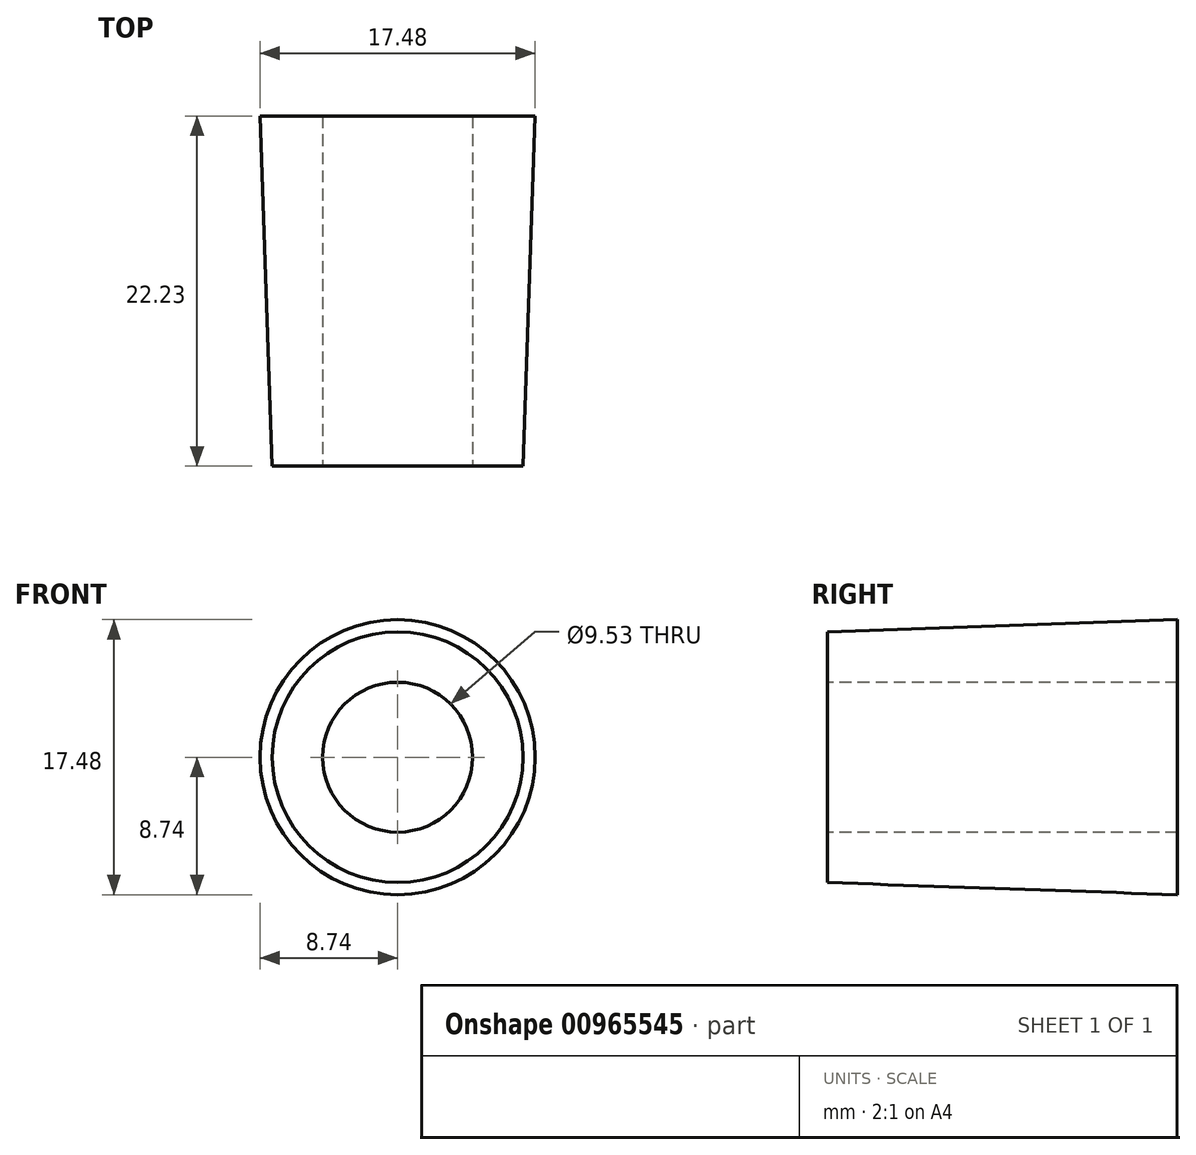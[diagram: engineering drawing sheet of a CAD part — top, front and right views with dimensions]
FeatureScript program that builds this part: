
annotation { "Feature Type Name" : "Feature", "Feature Type Description" : "" }
export const myFeature = defineFeature(function(context is Context, id is Id, definition is map)
    precondition{}
    {
        {
            var Q0;
            Q0=qCreatedBy(makeId("Right.planeOp"),FACE);
            var sketch = newSketch(context, id + "F0", { "sketchPlane" : qUnion([Q0])});
            skLineSegment(sketch, "E0", {"start": v(5.87, 0) * mm, "end": v(165.81, 0) * mm, "construction": true});
            skLineSegment(sketch, "E1", {"start": v(0, 4.76) * mm, "end": v(0, 7.96) * mm});
            skLineSegment(sketch, "E2", {"start": v(0, 7.96) * mm, "end": v(22.22, 8.74) * mm});
            skLineSegment(sketch, "E3", {"start": v(22.23, 8.74) * mm, "end": v(22.23, 4.76) * mm});
            skLineSegment(sketch, "E4", {"start": v(22.23, 4.76) * mm, "end": v(0, 4.76) * mm});
            skSolve(sketch);
        }
        {
            var Q0;
            Q0 = qSketchRegion(id + "F0", true);
            var Q1;
            Q1=sQuery(id+"F0.wireOp",EDGE,"E0");
            revolve(context, id + "F1", {"surfaceOperationType" : NewSurfaceOperationType.NEW, "entities" : qUnion([Q0]), "axis" : qUnion([Q1]), "revolveType" : RevolveType.FULL});
        }
    });
